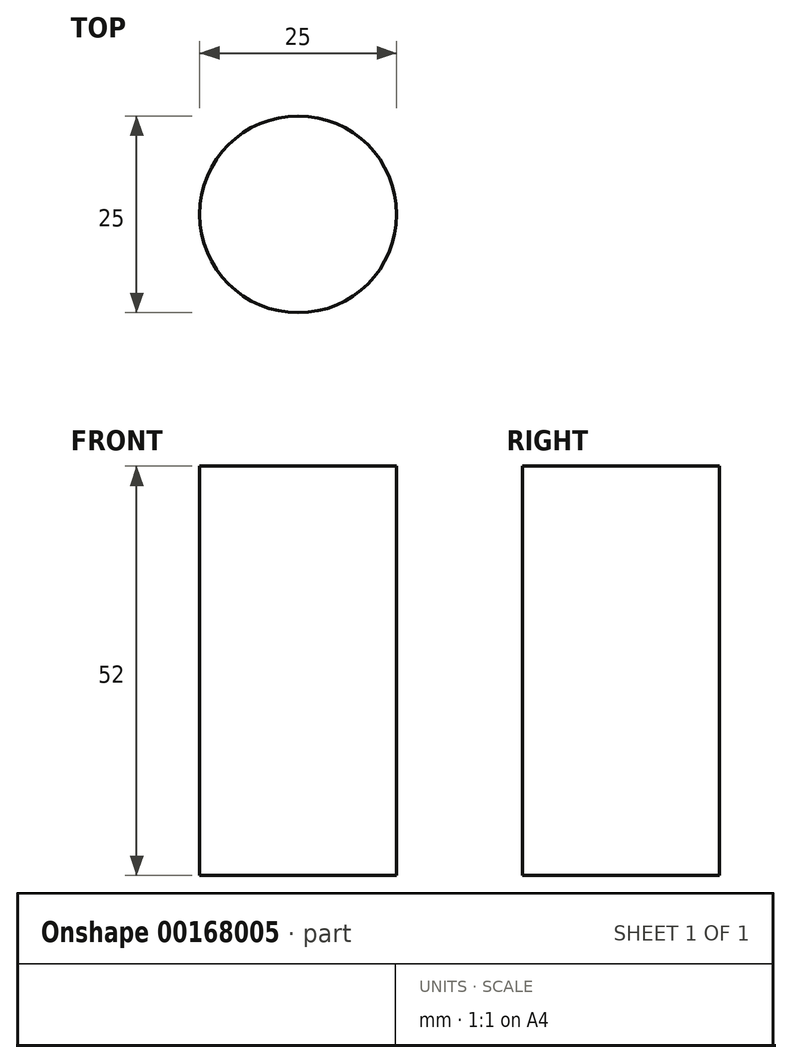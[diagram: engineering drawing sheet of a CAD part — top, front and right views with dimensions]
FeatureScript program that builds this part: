
annotation { "Feature Type Name" : "Feature", "Feature Type Description" : "" }
export const myFeature = defineFeature(function(context is Context, id is Id, definition is map)
    precondition{}
    {
        {
            var Q0;
            Q0=qCreatedBy(makeId("Top.planeOp"),FACE);
            var sketch = newSketch(context, id + "F0", { "sketchPlane" : qUnion([Q0])});
            skCircle(sketch, "E0", {"center": v(0, 0) * mm, "radius": 12.5 * mm});
            skSolve(sketch);
        }
        {
            var Q0;
            Q0=qSketchRegion(id+"F0",true);
            extrude(context, id + "F1", {"entities" : qUnion([Q0]), "depth" : 52 * mm, "symmetric" : true});
        }
    });
